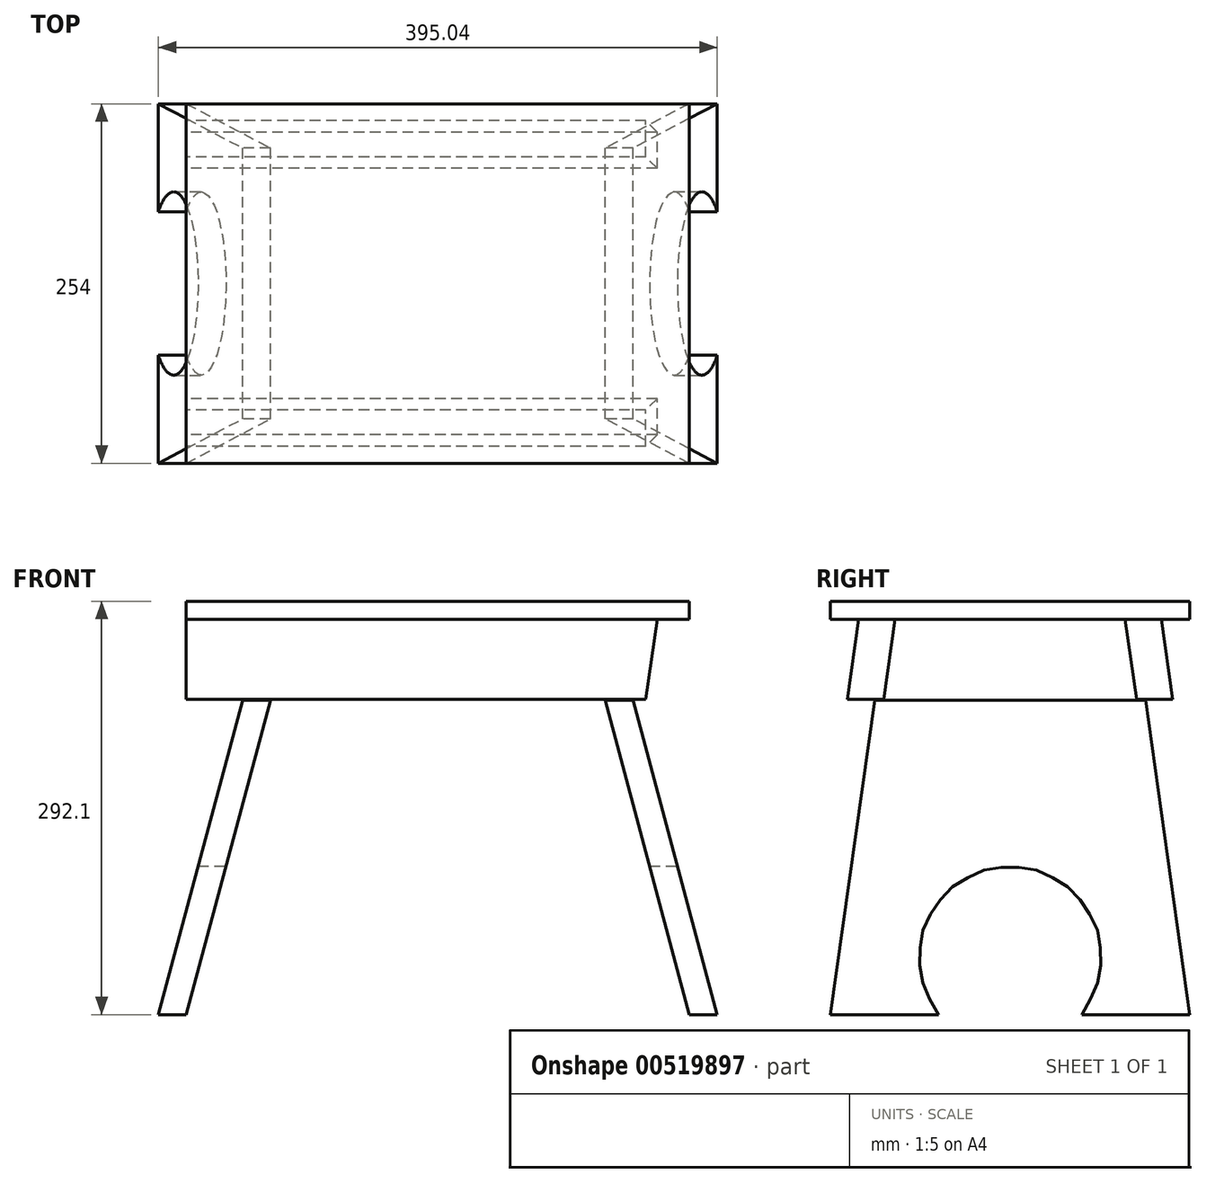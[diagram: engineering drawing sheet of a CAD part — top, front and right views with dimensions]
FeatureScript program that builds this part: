
annotation { "Feature Type Name" : "Feature", "Feature Type Description" : "" }
export const myFeature = defineFeature(function(context is Context, id is Id, definition is map)
    precondition{}
    {
        {
            var Q0;
            Q0=qCreatedBy(makeId("Front.planeOp"),FACE);
            var sketch = newSketch(context, id + "F0", { "sketchPlane" : qUnion([Q0])});
            skPoint(sketch, "E0.middle", {"position": v(0, 0) * mm});
            skLineSegment(sketch, "E1.bottom", {"start": v(177.8, 6.35) * mm, "end": v(-177.8, 6.35) * mm});
            skLineSegment(sketch, "E1.top", {"start": v(177.8, -6.35) * mm, "end": v(-177.8, -6.35) * mm});
            skLineSegment(sketch, "E1.left", {"start": v(177.8, 6.35) * mm, "end": v(177.8, -6.35) * mm});
            skLineSegment(sketch, "E1.right", {"start": v(-177.8, 6.35) * mm, "end": v(-177.8, -6.35) * mm});
            skLineSegment(sketch, "E2.bottom", {"start": v(177.8, -6.35) * mm, "end": v(-177.8, -6.35) * mm, "construction": true});
            skLineSegment(sketch, "E2.top", {"start": v(177.8, -285.75) * mm, "end": v(-177.8, -285.75) * mm, "construction": true});
            skLineSegment(sketch, "E2.left", {"start": v(177.8, -6.35) * mm, "end": v(177.8, -285.75) * mm, "construction": true});
            skLineSegment(sketch, "E2.right", {"start": v(-177.8, -6.35) * mm, "end": v(-177.8, -285.75) * mm, "construction": true});
            skLineSegment(sketch, "E3.bottom", {"start": v(0, -6.35) * mm, "end": v(0.26, -6.35) * mm, "construction": true});
            skLineSegment(sketch, "E3.top", {"start": v(0, -285.75) * mm, "end": v(0, -285.75) * mm});
            skLineSegment(sketch, "E4", {"start": v(0, 0) * mm, "end": v(0, -285.75) * mm, "construction": true});
            skLineSegment(sketch, "E5.bottom", {"start": v(-177.8, -6.35) * mm, "end": v(177.8, -6.35) * mm});
            skLineSegment(sketch, "E5.top", {"start": v(-177.8, -63.67) * mm, "end": v(177.8, -63.67) * mm});
            skLineSegment(sketch, "E5.left", {"start": v(-177.8, -6.35) * mm, "end": v(-177.8, -63.67) * mm});
            skLineSegment(sketch, "E5.right", {"start": v(177.8, -6.35) * mm, "end": v(177.8, -63.67) * mm});
            skLineSegment(sketch, "E6", {"start": v(102.93, -6.35) * mm, "end": v(177.8, -285.75) * mm});
            skLineSegment(sketch, "E7", {"start": v(122.66, -6.35) * mm, "end": v(197.52, -285.75) * mm});
            skLineSegment(sketch, "E8.MirrorCS", {"start": v(-122.66, -6.35) * mm, "end": v(-197.52, -285.75) * mm});
            skLineSegment(sketch, "E9.MirrorCS", {"start": v(-102.93, -6.35) * mm, "end": v(-177.8, -285.75) * mm});
            skLineSegment(sketch, "E10", {"start": v(-197.52, -285.75) * mm, "end": v(-177.8, -285.75) * mm});
            skLineSegment(sketch, "E11", {"start": v(197.52, -285.75) * mm, "end": v(177.8, -285.75) * mm});
            skLineSegment(sketch, "E12", {"start": v(-155.03, -6.35) * mm, "end": v(-146.98, -63.67) * mm});
            skLineSegment(sketch, "E13.MirrorCS", {"start": v(155.03, -6.35) * mm, "end": v(146.98, -63.67) * mm});
            skSolve(sketch);
        }
        {
            var Q0;
            Q0=makeQuery(id+"F0.imprint","IMPRINT",FACE,{"disambiguationData":[TD([[makeQuery(id+"F0.imprint","IMPRINT",EDGE,{"derivedFrom":sQuery(id+"F0.wireOp",EDGE,"E1.bottom")}),1.0]])]});
            extrude(context, id + "F1", {"entities" : qUnion([Q0]), "endBound" : BoundingType.SYMMETRIC, "depth" : 254 * mm, "offsetDistance" : 25.4 * mm, "hasDraft" : true, "draftAngle" : 0 * degree});
        }
        {
            var Q0;
            Q0=makeQuery(id+"F0.imprint","IMPRINT",FACE,{"disambiguationData":[TD([[makeQuery(id+"F0.imprint","IMPRINT",EDGE,{"derivedFrom":sQuery(id+"F0.wireOp",EDGE,"E1.bottom")}),1.0]])]});
            extrude(context, id + "F2", {"entities" : qUnion([Q0]), "operationType" : NewBodyOperationType.ADD, "endBound" : BoundingType.SYMMETRIC, "depth" : 254 * mm, "offsetDistance" : 25.4 * mm});
        }
        {
            var Q0;
            {var subQ0=sQuery(id+"F0.wireOp",EDGE,"E8.MirrorCS");var subQ1=sQuery(id+"F0.wireOp",EDGE,"E5.bottom");var subQ2=makeQuery(id+"F0.imprint","INTERSECT",VERTEX,{"derivedFrom":[subQ1,subQ0]});Q0=makeQuery(id+"F0.imprint","IMPRINT",FACE,{"disambiguationData":[TD([[makeQuery(id+"F0.imprint","IMPRINT",EDGE,{"disambiguationData":[TD([[subQ2,-1.0]])],"derivedFrom":subQ1}),-1.0]])]});}
            var Q1;
            {var subQ5=sQuery(id+"F0.wireOp",EDGE,"E10");Q1=makeQuery(id+"F0.imprint","IMPRINT",FACE,{"disambiguationData":[TD([[makeQuery(id+"F0.imprint","IMPRINT",EDGE,{"derivedFrom":subQ5}),1.0]])]});}
            var Q2;
            {var subQ0=sQuery(id+"F0.wireOp",EDGE,"E6");var subQ1=sQuery(id+"F0.wireOp",EDGE,"E5.bottom");var subQ2=makeQuery(id+"F0.imprint","INTERSECT",VERTEX,{"derivedFrom":[subQ1,subQ0]});Q2=makeQuery(id+"F0.imprint","IMPRINT",FACE,{"disambiguationData":[TD([[makeQuery(id+"F0.imprint","IMPRINT",EDGE,{"disambiguationData":[TD([[subQ2,-1.0]])],"derivedFrom":subQ1}),-1.0]])]});}
            var Q3;
            {var subQ5=sQuery(id+"F0.wireOp",EDGE,"E11");Q3=makeQuery(id+"F0.imprint","IMPRINT",FACE,{"disambiguationData":[TD([[makeQuery(id+"F0.imprint","IMPRINT",EDGE,{"derivedFrom":subQ5}),-1.0]])]});}
            var Q4;
            Q4=makeQuery(id+"F1.opExtrude","CAP_FACE",FACE,{"disambiguationData":[OSD([sQuery(id+"F0.wireOp",EDGE,"E1.bottom"),sQuery(id+"F0.wireOp",EDGE,"E1.left"),sQuery(id+"F0.wireOp",EDGE,"E1.right"),sQuery(id+"F0.wireOp",EDGE,"E5.bottom")])],"isStart":false});
            var Q5;
            Q5=makeQuery(id+"F1.opExtrude","CAP_VERTEX",VERTEX,{"disambiguationData":[OSD([sQuery(id+"F0.wireOp",EDGE,"E1.left"),sQuery(id+"F0.wireOp",EDGE,"E5.bottom"),sQuery(id+"F0.wireOp",EDGE,"E5.right"),sQuery(id+"F0.wireOp",EDGE,"XrIPzr6K-PRgp-dWhc-1EyD-QsXbtfm9q2Iy")])],"isStart":true});
            var Q6;
            Q6=makeQuery(id+"F1.opExtrude","CAP_FACE",FACE,{"disambiguationData":[OSD([sQuery(id+"F0.wireOp",EDGE,"E1.bottom"),sQuery(id+"F0.wireOp",EDGE,"E1.left"),sQuery(id+"F0.wireOp",EDGE,"E1.right"),sQuery(id+"F0.wireOp",EDGE,"E5.bottom")])],"isStart":true});
            extrude(context, id + "F3", {"entities" : qUnion([Q0, Q1, Q2, Q3]), "endBound" : BoundingType.UP_TO_SURFACE, "depth" : 25.4 * mm, "endBoundEntityFace" : qUnion([Q4]), "endBoundEntityVertex" : qUnion([Q5]), "offsetDistance" : 25.4 * mm, "hasSecondDirection" : true, "secondDirectionBound" : SecondDirectionBoundingType.UP_TO_SURFACE, "secondDirectionOppositeDirection" : true, "secondDirectionDepth" : 25.4 * mm, "secondDirectionBoundEntityFace" : qUnion([Q6])});
        }
        {
            var Q0;
            Q0=qCreatedBy(makeId("Right.planeOp"),FACE);
            var sketch = newSketch(context, id + "F4", { "sketchPlane" : qUnion([Q0])});
            skLineSegment(sketch, "E14.0.0", {"start": v(-127, -6.35) * mm, "end": v(-127, -285.75) * mm});
            skLineSegment(sketch, "E14.0.1", {"start": v(-127, -285.75) * mm, "end": v(127, -285.75) * mm});
            skLineSegment(sketch, "E14.0.2", {"start": v(127, -285.75) * mm, "end": v(127, -6.35) * mm});
            skLineSegment(sketch, "E14.0.3", {"start": v(127, -6.35) * mm, "end": v(-127, -6.35) * mm});
            skLineSegment(sketch, "E15", {"start": v(-127, -285.75) * mm, "end": v(-87.73, -6.35) * mm});
            skLineSegment(sketch, "E16", {"start": v(127, -285.75) * mm, "end": v(87.73, -6.35) * mm});
            skArc(sketch, "E17", {"start": v(50.72, -285.75) * mm, "mid": v(0, -180.63) * mm, "end": v(-50.72, -285.75) * mm});
            skSolve(sketch);
        }
        {
            var Q0;
            Q0=qCreatedBy(makeId("Right.planeOp"),FACE);
            var sketch = newSketch(context, id + "F5", { "sketchPlane" : qUnion([Q0])});
            skLineSegment(sketch, "E18.0", {"start": v(-127, -285.75) * mm, "end": v(-87.73, -6.35) * mm});
            skLineSegment(sketch, "E19.0", {"start": v(127, -6.35) * mm, "end": v(-127, -6.35) * mm});
            skLineSegment(sketch, "E20.0", {"start": v(127, -285.75) * mm, "end": v(87.73, -6.35) * mm});
            skLineSegment(sketch, "E21", {"start": v(-106.97, -6.35) * mm, "end": v(-114.95, -63.1) * mm});
            skLineSegment(sketch, "E22", {"start": v(0, -6.35) * mm, "end": v(0, -87.62) * mm});
            skLineSegment(sketch, "E23.MirrorCS", {"start": v(81.32, -6.35) * mm, "end": v(89.3, -63.1) * mm});
            skLineSegment(sketch, "E24.MirrorCS", {"start": v(106.97, -6.35) * mm, "end": v(114.95, -63.1) * mm});
            skLineSegment(sketch, "E25.MirrorCS", {"start": v(-81.32, -6.35) * mm, "end": v(-89.3, -63.1) * mm});
            skLineSegment(sketch, "E26", {"start": v(-114.95, -63.1) * mm, "end": v(-89.3, -63.1) * mm});
            skLineSegment(sketch, "E27", {"start": v(89.3, -63.1) * mm, "end": v(114.95, -63.1) * mm});
            skSolve(sketch);
        }
        {
            var Q0;
            {var subQ0=sQuery(id+"F4.wireOp",EDGE,"E14.0.0");Q0=makeQuery(id+"F4.imprint","IMPRINT",FACE,{"disambiguationData":[TD([[makeQuery(id+"F4.imprint","IMPRINT",EDGE,{"derivedFrom":subQ0}),1.0]])]});}
            var Q1;
            {var subQ0=sQuery(id+"F4.wireOp",EDGE,"E14.0.2");Q1=makeQuery(id+"F4.imprint","IMPRINT",FACE,{"disambiguationData":[TD([[makeQuery(id+"F4.imprint","IMPRINT",EDGE,{"derivedFrom":subQ0}),1.0]])]});}
            var Q2;
            {var subQ0=sQuery(id+"F4.wireOp",EDGE,"E17");Q2=makeQuery(id+"F4.imprint","IMPRINT",FACE,{"disambiguationData":[TD([[makeQuery(id+"F4.imprint","IMPRINT",EDGE,{"derivedFrom":subQ0}),1.0]])]});}
            extrude(context, id + "F6", {"entities" : qUnion([Q0, Q1, Q2]), "operationType" : NewBodyOperationType.REMOVE, "endBound" : BoundingType.THROUGH_ALL, "oppositeDirection" : true, "depth" : 25.4 * mm, "offsetDistance" : 25.4 * mm, "hasSecondDirection" : true, "secondDirectionBound" : SecondDirectionBoundingType.THROUGH_ALL, "secondDirectionOppositeDirection" : false, "secondDirectionDepth" : 25.4 * mm});
        }
        {
            var Q0;
            {var subQ5=sQuery(id+"F5.wireOp",EDGE,"E21");Q0=makeQuery(id+"F5.imprint","IMPRINT",FACE,{"disambiguationData":[TD([[makeQuery(id+"F5.imprint","IMPRINT",EDGE,{"derivedFrom":subQ5}),1.0]])]});}
            var Q1;
            {var subQ3=sQuery(id+"F5.wireOp",EDGE,"E24.MirrorCS");Q1=makeQuery(id+"F5.imprint","IMPRINT",FACE,{"disambiguationData":[TD([[makeQuery(id+"F5.imprint","IMPRINT",EDGE,{"derivedFrom":subQ3}),-1.0]])]});}
            var Q2;
            {var subQ5=sQuery(id+"F5.wireOp",EDGE,"E25.MirrorCS");Q2=makeQuery(id+"F5.imprint","IMPRINT",FACE,{"disambiguationData":[TD([[makeQuery(id+"F5.imprint","IMPRINT",EDGE,{"derivedFrom":subQ5}),-1.0]])]});}
            var Q3;
            {var subQ3=sQuery(id+"F5.wireOp",EDGE,"E23.MirrorCS");Q3=makeQuery(id+"F5.imprint","IMPRINT",FACE,{"disambiguationData":[TD([[makeQuery(id+"F5.imprint","IMPRINT",EDGE,{"derivedFrom":subQ3}),1.0]])]});}
            var Q4;
            {var subQ0=makeQuery(id+"F1.opExtrude","SWEPT_FACE",FACE,{"disambiguationData":[OSD([sQuery(id+"F0.wireOp",EDGE,"E1.left")])]});Q4=makeQuery(id+"F1.*.booleanUnion.opBoolean","MERGE",FACE,{"derivedFrom":[makeQuery(id+"F1.*.split.splitOp","SPLIT",FACE,{"derivedFrom":subQ0}),makeQuery(id+"F1.*.split.splitOp","SPLIT",FACE,{"derivedFrom":subQ0,"isFromBackBody":true})]});}
            var Q5;
            {var subQ0=makeQuery(id+"F1.opExtrude","SWEPT_FACE",FACE,{"disambiguationData":[OSD([sQuery(id+"F0.wireOp",EDGE,"E1.right")])]});Q5=makeQuery(id+"F1.*.booleanUnion.opBoolean","MERGE",FACE,{"derivedFrom":[makeQuery(id+"F1.*.split.splitOp","SPLIT",FACE,{"derivedFrom":subQ0}),makeQuery(id+"F1.*.split.splitOp","SPLIT",FACE,{"derivedFrom":subQ0,"isFromBackBody":true})]});}
            extrude(context, id + "F7", {"entities" : qUnion([Q0, Q1, Q2, Q3]), "endBound" : BoundingType.UP_TO_SURFACE, "depth" : 25.4 * mm, "endBoundEntityFace" : qUnion([Q4]), "offsetDistance" : 25.4 * mm, "hasSecondDirection" : true, "secondDirectionBound" : SecondDirectionBoundingType.UP_TO_SURFACE, "secondDirectionOppositeDirection" : true, "secondDirectionDepth" : 25.4 * mm, "secondDirectionBoundEntityFace" : qUnion([Q5])});
        }
        {
            var Q0;
            {var subQ0=sQuery(id+"F0.wireOp",EDGE,"E5.left");Q0=makeQuery(id+"F0.imprint","IMPRINT",FACE,{"disambiguationData":[TD([[makeQuery(id+"F0.imprint","IMPRINT",EDGE,{"derivedFrom":subQ0}),1.0]])]});}
            var Q1;
            {var subQ0=sQuery(id+"F0.wireOp",EDGE,"E5.right");Q1=makeQuery(id+"F0.imprint","IMPRINT",FACE,{"disambiguationData":[TD([[makeQuery(id+"F0.imprint","IMPRINT",EDGE,{"derivedFrom":subQ0}),-1.0]])]});}
            extrude(context, id + "F8", {"entities" : qUnion([Q0, Q1]), "operationType" : NewBodyOperationType.REMOVE, "endBound" : BoundingType.THROUGH_ALL, "depth" : 25.4 * mm, "offsetDistance" : 25.4 * mm, "hasSecondDirection" : true, "secondDirectionBound" : SecondDirectionBoundingType.THROUGH_ALL, "secondDirectionOppositeDirection" : true, "secondDirectionDepth" : 25.4 * mm});
        }
        {
            var Q0;
            Q0=makeQuery(id+"F3.opExtrude","SWEPT_BODY",BODY,{"disambiguationData":[OSD([sQuery(id+"F0.wireOp",EDGE,"E5.bottom"),sQuery(id+"F0.wireOp",EDGE,"E8.MirrorCS"),sQuery(id+"F0.wireOp",EDGE,"E9.MirrorCS"),sQuery(id+"F0.wireOp",EDGE,"E10")])]});
            var Q1;
            Q1=makeQuery(id+"F3.opExtrude","SWEPT_BODY",BODY,{"disambiguationData":[OSD([sQuery(id+"F0.wireOp",EDGE,"E5.bottom"),sQuery(id+"F0.wireOp",EDGE,"E6"),sQuery(id+"F0.wireOp",EDGE,"E7"),sQuery(id+"F0.wireOp",EDGE,"E11")])]});
            var Q2;
            Q2=makeQuery(id+"F7.opExtrude","SWEPT_BODY",BODY,{"disambiguationData":[OSD([sQuery(id+"F5.wireOp",EDGE,"E19.0"),sQuery(id+"F5.wireOp",EDGE,"E23.MirrorCS"),sQuery(id+"F5.wireOp",EDGE,"E24.MirrorCS"),sQuery(id+"F5.wireOp",EDGE,"E27")])]});
            var Q3;
            Q3=makeQuery(id+"F7.opExtrude","SWEPT_BODY",BODY,{"disambiguationData":[OSD([sQuery(id+"F5.wireOp",EDGE,"E19.0"),sQuery(id+"F5.wireOp",EDGE,"E21"),sQuery(id+"F5.wireOp",EDGE,"E25.MirrorCS"),sQuery(id+"F5.wireOp",EDGE,"E26")])]});
            booleanBodies(context, id + "F9", {"operationType" : BooleanOperationType.SUBTRACTION, "tools" : qUnion([Q0, Q1]), "targets" : qUnion([Q2, Q3]), "keepTools" : true});
        }
    });
